FCSTD DOCUMENT  (FreeCAD 0.16R4924 (Git))
Label: montez_YZplate
License: All rights reserved
LicenseURL: http://en.wikipedia.org/wiki/All_rights_reserved
objects: Sketcher::SketchObject×1
note: 1 computed .brp shape members not serialized (recipe doc carries the construction recipe); baked Part::Feature solids carry a one-line shape summary decoded from their .brp

FEATURE [Sketcher::SketchObject] Sketch
  sketch-geometry (50):
    g0: Circle CenterX=104.35 CenterY=53.5 CenterZ=0 NormalX=0 NormalY=0 NormalZ=1 Radius=11.5
    g1: Circle [constr] CenterX=44.35 CenterY=23.5 CenterZ=0 NormalX=0 NormalY=0 NormalZ=1 Radius=4
    g2: Circle [constr] CenterX=114.35 CenterY=23.5 CenterZ=0 NormalX=0 NormalY=0 NormalZ=1 Radius=4
    g3: LineSegment [constr] StartX=44.35 StartY=23.5 StartZ=0 EndX=114.35 EndY=23.5 EndZ=0
    g4: LineSegment [constr] StartX=104.35 StartY=53.5 StartZ=0 EndX=104.35 EndY=23.5 EndZ=0
    g5: LineSegment [constr] StartX=119.85 StartY=69 StartZ=0 EndX=88.85 EndY=38 EndZ=0
    g6: LineSegment [constr] StartX=88.85 StartY=69 StartZ=0 EndX=119.85 EndY=38 EndZ=0
    g7: LineSegment [constr] StartX=88.85 StartY=69 StartZ=0 EndX=119.85 EndY=69 EndZ=0
    g8: LineSegment [constr] StartX=119.85 StartY=69 StartZ=0 EndX=119.85 EndY=38 EndZ=0
    g9: LineSegment [constr] StartX=119.85 StartY=38 StartZ=0 EndX=88.85 EndY=38 EndZ=0
    g10: LineSegment [constr] StartX=88.85 StartY=38 StartZ=0 EndX=88.85 EndY=69 EndZ=0
    g11: Circle CenterX=88.85 CenterY=69 CenterZ=0 NormalX=0 NormalY=0 NormalZ=1 Radius=1.75
    g12: Circle CenterX=119.85 CenterY=69 CenterZ=0 NormalX=0 NormalY=0 NormalZ=1 Radius=1.75
    g13: Circle CenterX=88.85 CenterY=38 CenterZ=0 NormalX=0 NormalY=0 NormalZ=1 Radius=1.75
    g14: Circle CenterX=119.85 CenterY=38 CenterZ=0 NormalX=0 NormalY=0 NormalZ=1 Radius=1.75
    g15: LineSegment StartX=39.4431 StartY=24.25 StartZ=0 EndX=44.35 EndY=29.1569 EndZ=0
    g16: LineSegment StartX=44.35 StartY=29.1569 StartZ=0 EndX=49.2569 EndY=24.25 EndZ=0
    g17: LineSegment StartX=49.2569 StartY=24.25 StartZ=0 EndX=109.443 EndY=24.25 EndZ=0
    g18: LineSegment StartX=109.443 StartY=24.25 StartZ=0 EndX=114.35 EndY=29.1569 EndZ=0
    g19: LineSegment StartX=114.35 StartY=29.1569 StartZ=0 EndX=119.257 EndY=24.25 EndZ=0
    g20: LineSegment StartX=131.85 StartY=24.25 StartZ=0 EndX=131.85 EndY=81 EndZ=0
    g21: LineSegment StartX=131.85 StartY=81 StartZ=0 EndX=26.85 EndY=81 EndZ=0
    g22: LineSegment StartX=26.85 StartY=81 StartZ=0 EndX=26.85 EndY=24.25 EndZ=0
    g23: LineSegment StartX=26.85 StartY=24.25 StartZ=0 EndX=39.4431 EndY=24.25 EndZ=0
    g24: LineSegment [constr] StartX=39.4431 StartY=24.25 StartZ=0 EndX=49.2569 EndY=24.25 EndZ=0
    g25: LineSegment [constr] StartX=109.443 StartY=24.25 StartZ=0 EndX=119.257 EndY=24.25 EndZ=0
    g26: LineSegment StartX=119.257 StartY=24.25 StartZ=0 EndX=131.85 EndY=24.25 EndZ=0
    g27: LineSegment [constr] StartX=119.257 StartY=24.25 StartZ=0 EndX=119.257 EndY=22.75 EndZ=0
    g28: LineSegment [constr] StartX=126.85 StartY=22.75 StartZ=0 EndX=119.257 EndY=22.75 EndZ=0
    g29: LineSegment [constr] StartX=119.257 StartY=22.75 StartZ=0 EndX=114.35 EndY=17.8431 EndZ=0
    g30: LineSegment [constr] StartX=114.35 StartY=17.8431 StartZ=0 EndX=109.443 EndY=22.75 EndZ=0
    g31: LineSegment [constr] StartX=109.443 StartY=22.75 StartZ=0 EndX=101.85 EndY=22.75 EndZ=0
    g32: LineSegment [constr] StartX=101.85 StartY=22.75 StartZ=0 EndX=101.85 EndY=14.8431 EndZ=0
    g33: LineSegment [constr] StartX=101.85 StartY=14.8431 StartZ=0 EndX=126.85 EndY=14.8431 EndZ=0
    g34: LineSegment [constr] StartX=126.85 StartY=14.8431 StartZ=0 EndX=126.85 EndY=22.75 EndZ=0
    g35: LineSegment [constr] StartX=109.443 StartY=22.75 StartZ=0 EndX=119.257 EndY=22.75 EndZ=0
    g36: LineSegment [constr] StartX=31.85 StartY=22.75 StartZ=0 EndX=39.4431 EndY=22.75 EndZ=0
    g37: LineSegment [constr] StartX=39.4431 StartY=22.75 StartZ=0 EndX=49.2569 EndY=22.75 EndZ=0
    g38: LineSegment [constr] StartX=49.2569 StartY=22.75 StartZ=0 EndX=56.85 EndY=22.75 EndZ=0
    g39: LineSegment [constr] StartX=56.85 StartY=22.75 StartZ=0 EndX=56.85 EndY=14.8431 EndZ=0
    g40: LineSegment [constr] StartX=56.85 StartY=14.8431 StartZ=0 EndX=31.85 EndY=14.8431 EndZ=0
    g41: LineSegment [constr] StartX=31.85 StartY=14.8431 StartZ=0 EndX=31.85 EndY=22.75 EndZ=0
    g42: LineSegment [constr] StartX=39.4431 StartY=22.75 StartZ=0 EndX=44.35 EndY=17.8431 EndZ=0
    g43: LineSegment [constr] StartX=44.35 StartY=17.8431 StartZ=0 EndX=49.2569 EndY=22.75 EndZ=0
    g44: LineSegment [constr] StartX=39.4431 StartY=24.25 StartZ=0 EndX=39.4431 EndY=22.75 EndZ=0
    g45: LineSegment [constr] StartX=125.85 StartY=32 StartZ=0 EndX=125.85 EndY=75 EndZ=0
    g46: LineSegment [constr] StartX=125.85 StartY=75 StartZ=0 EndX=82.85 EndY=75 EndZ=0
    g47: LineSegment [constr] StartX=82.85 StartY=75 StartZ=0 EndX=82.85 EndY=32 EndZ=0
    g48: LineSegment [constr] StartX=82.85 StartY=32 StartZ=0 EndX=125.85 EndY=32 EndZ=0
    g49: Circle [constr] CenterX=104.35 CenterY=53.5 CenterZ=0 NormalX=0 NormalY=0 NormalZ=1 Radius=21.5
  constraints (138):
    c: Coincident(g3,g1)
    c: Coincident(g3,g2)
    c: Horizontal(g3)
    c: Distance(g3) = 70
    c: Coincident(g4,g0)
    c: PointOnObject(g4,g3)
    c: Vertical(g4)
    c: PointOnObject(g0,g5)
    c: PointOnObject(g0,g6)
    c: Coincident(g7,g8)
    c: Coincident(g8,g9)
    c: Coincident(g9,g10)
    c: Coincident(g10,g7)
    c: Horizontal(g7)
    c: Horizontal(g9)
    c: Vertical(g8)
    c: Vertical(g10)
    c: Coincident(g7,g6)
    c: Coincident(g8,g6)
    c: Coincident(g5,g9)
    c: Coincident(g5,g7)
    c: Distance(g7) = 31
    c: Equal(g8,g7)
    c: Distance(g4) = 30
    c: Coincident(g11,g6)
    c: Coincident(g12,g5)
    c: Coincident(g13,g5)
    c: Equal(g12,g11)
    c: Equal(g11,g13)
    c: Equal(g13,g14)
    c: Radius(g11) = 1.75
    c: Radius(g1) = 4
    c: Equal(g2,g1)
    c: Coincident(g6,g14)
    c: Distance(g2,g4) = 10
    c: Coincident(g15,g16)
    c: Coincident(g16,g17)
    c: Horizontal(g17)
    c: Coincident(g17,g18)
    c: Coincident(g18,g19)
    c: Vertical(g20)
    c: Coincident(g20,g21)
    c: Horizontal(g21)
    c: Coincident(g21,g22)
    c: Vertical(g22)
    c: Coincident(g22,g23)
    c: Coincident(g23,g15)
    c: Horizontal(g23)
    c: Tangent(g15,g1)
    c: Perpendicular(g15,g16)
    c: Tangent(g16,g1)
    c: Equal(g15,g16)
    c: Coincident(g24,g15)
    c: Coincident(g24,g16)
    c: Horizontal(g24)
    c: Coincident(g25,g17)
    c: Coincident(g25,g19)
    c: Horizontal(g25)
    c: Coincident(g26,g19)
    c: Coincident(g26,g20)
    c: Horizontal(g26)
    c: Equal(g18,g19)
    c: Equal(g18,g19)
    c: Perpendicular(g18,g19)
    c: Tangent(g18,g2)
    c: Tangent(g19,g2)
    c: Coincident(g27,g19)
    c: Vertical(g27)
    c: Coincident(g28,g27)
    c: Horizontal(g28)
    c: Coincident(g28,g29)
    c: Coincident(g29,g30)
    c: Coincident(g30,g31)
    c: Horizontal(g31)
    c: Coincident(g31,g32)
    c: Vertical(g32)
    c: Coincident(g32,g33)
    c: Horizontal(g33)
    c: Coincident(g33,g34)
    c: Coincident(g34,g28)
    c: Vertical(g34)
    c: Equal(g29,g30)
    c: Coincident(g35,g30)
    c: Coincident(g35,g27)
    c: Horizontal(g35)
    c: Tangent(g30,g2)
    c: Tangent(g29,g2)
    c: Perpendicular(g30,g29)
    c: Distance(g27) = 1.5
    c: Distance(g29,g33) = 3
    c: Horizontal(g36)
    c: Coincident(g36,g37)
    c: Horizontal(g37)
    c: Coincident(g37,g38)
    c: Horizontal(g38)
    c: Coincident(g38,g39)
    c: Vertical(g39)
    c: Coincident(g39,g40)
    c: Horizontal(g40)
    c: Coincident(g40,g41)
    c: Coincident(g41,g36)
    c: Vertical(g41)
    c: Coincident(g36,g42)
    c: Tangent(g42,g1)
    c: Coincident(g42,g43)
    c: Coincident(g37,g43)
    c: Perpendicular(g43,g42)
    c: Tangent(g43,g1)
    c: Equal(g43,g42)
    c: Coincident(g44,g15)
    c: Coincident(g44,g36)
    c: Vertical(g44)
    c: Equal(g44,g27)
    c: Equal(g38,g36)
    c: Equal(g32,g39)
    c: Equal(g31,g28)
    c: Equal(g28,g38)
    c: Distance(g40) = 25
    c: Radius(g0) = 11.5
    c: Coincident(g45,g46)
    c: Coincident(g46,g47)
    c: Coincident(g47,g48)
    c: Coincident(g48,g45)
    c: Equal(g45,g46)
    c: Equal(g45,g47)
    c: Equal(g45,g48)
    c: Perpendicular(g45,g48)
    c: Horizontal(g46)
    c: Tangent(g49,g45)
    c: Tangent(g49,g46)
    c: Tangent(g49,g47)
    c: Distance(g46) = 43
    c: Coincident(g49,g0)
    c: DistanceX(g22,g36) = 5
    c: DistanceY(g45,g20) = 6
    c: DistanceX(g20,g28) = -5
    c: DistanceX(g22) = 26.85
    c: DistanceY(g22) = 24.25
